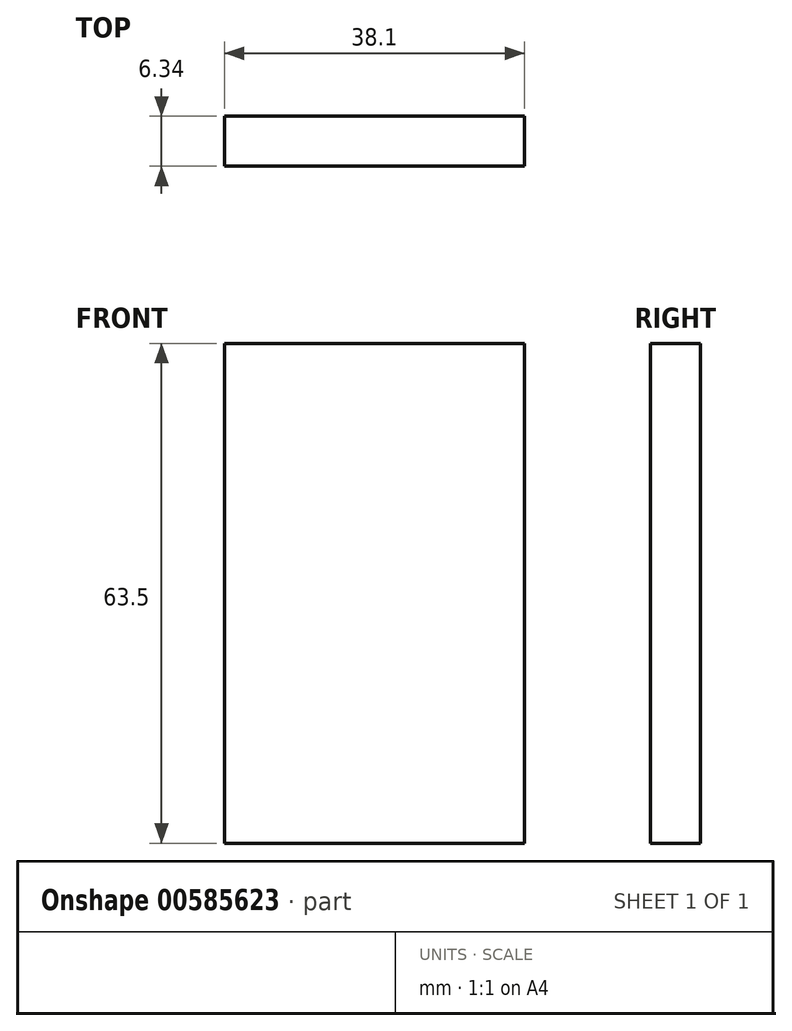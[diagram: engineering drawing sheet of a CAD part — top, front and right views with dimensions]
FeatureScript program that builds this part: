
annotation { "Feature Type Name" : "Feature", "Feature Type Description" : "" }
export const myFeature = defineFeature(function(context is Context, id is Id, definition is map)
    precondition{}
    {
        {
            var Q0;
            Q0=qCreatedBy(makeId("Top.planeOp"),FACE);
            var sketch = newSketch(context, id + "F0", { "sketchPlane" : qUnion([Q0])});
            skLineSegment(sketch, "E0.bottom", {"start": v(-19.05, 3.17) * mm, "end": v(19.05, 3.17) * mm});
            skLineSegment(sketch, "E0.top", {"start": v(-19.05, -3.18) * mm, "end": v(19.05, -3.18) * mm});
            skLineSegment(sketch, "E0.left", {"start": v(-19.05, 3.17) * mm, "end": v(-19.05, -3.18) * mm});
            skLineSegment(sketch, "E0.right", {"start": v(19.05, 3.17) * mm, "end": v(19.05, -3.18) * mm});
            skPoint(sketch, "E0.middle", {"position": v(0, 0) * mm});
            skSolve(sketch);
        }
        {
            var Q0;
            Q0=makeQuery(id+"F0.imprint","IMPRINT",FACE,{"disambiguationData":[TD([[makeQuery(id+"F0.imprint","IMPRINT",EDGE,{"derivedFrom":sQuery(id+"F0.wireOp",EDGE,"E0.bottom")}),-1.0]])]});
            extrude(context, id + "F1", {"entities" : qUnion([Q0]), "depth" : 63.5 * mm, "offsetDistance" : 25.4 * mm});
        }
    });
